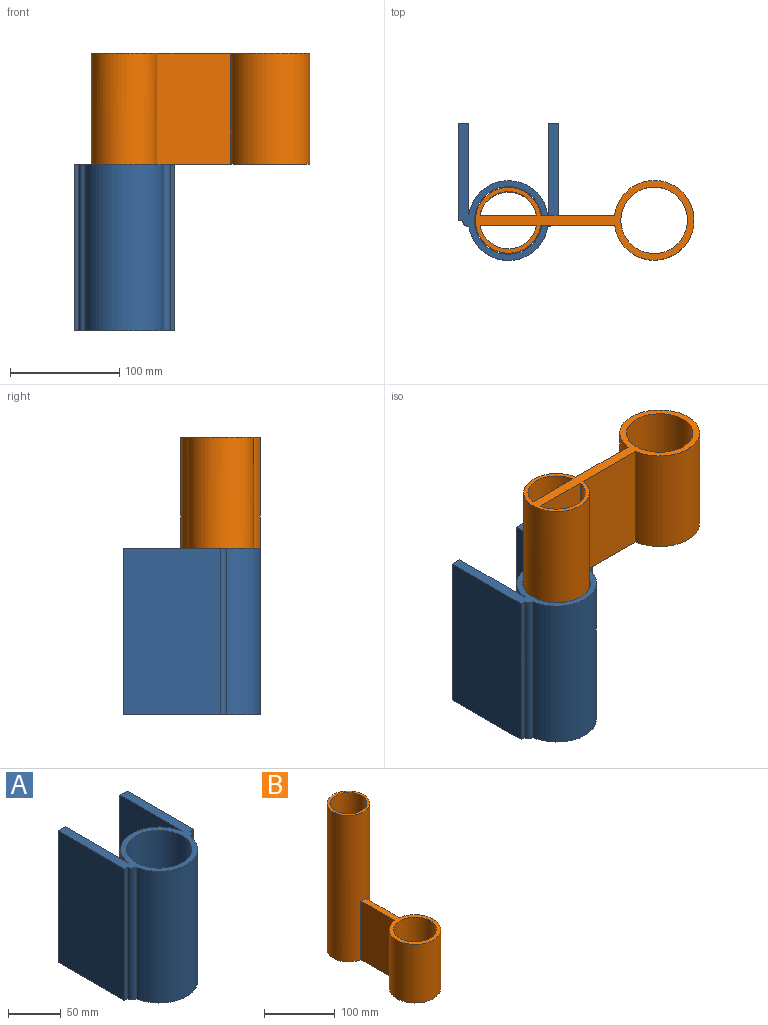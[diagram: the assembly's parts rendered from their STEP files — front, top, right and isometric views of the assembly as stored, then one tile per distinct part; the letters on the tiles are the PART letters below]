
ASSEMBLY  parts=2 mates=1
PART A: 17 faces, bbox 92.1x125.4x152.4 mm
  f0: cylinder r=36.51mm len=152.4mm, axis (0,0,1), area 15840.5mm2, adj f3,f9,f10,f16
  f1: cylinder r=30.96mm len=152.4mm, axis (0,0,1), area 29642.4mm2, adj f3,f16
  f2: cylinder r=36.51mm len=152.4mm, axis (0,0,1), area 15840.5mm2, adj f3,f4,f15,f16
  f3: plane 125.41x92.08mm, normal (0,0,-1), area 2919.4mm2, adj f0,f1,f2,f4,f5,f6,f7,f8
  f4: cylinder r=5.34mm len=152.4mm, axis (0,0,1), area 1335.1mm2, adj f2,f3,f5,f16
  f5: plane 152.4x4.2mm, normal (0,-1,0), area 640.5mm2, adj f3,f4,f8,f16
  f6: plane 152.4x83.56mm, normal (1,0,0), area 12734.6mm2, adj f3,f7,f9,f16
  f7: plane 152.4x9.53mm, normal (0,1,0), area 1451.6mm2, adj f3,f6,f8,f16
  f8: plane 152.4x88.9mm, normal (-1,0,0), area 13548.4mm2, adj f3,f5,f7,f16
  f9: cylinder r=5.34mm len=152.4mm, axis (0,0,1), area 59.6mm2, adj f0,f3,f6,f16
  f10: cylinder r=5.42mm len=152.4mm, axis (0,0,1), area 61.3mm2, adj f0,f3,f11,f16
  f11: plane 152.4x83.48mm, normal (-1,0,0), area 12722.9mm2, adj f3,f10,f14,f16
  f12: plane 152.4x4.11mm, normal (0,-1,0), area 626.2mm2, adj f3,f13,f15,f16
  f13: plane 152.4x88.9mm, normal (1,0,0), area 13548.4mm2, adj f3,f12,f14,f16
  f14: plane 152.4x9.53mm, normal (0,1,0), area 1451.6mm2, adj f3,f11,f13,f16
  f15: cylinder r=5.42mm len=152.4mm, axis (0,0,1), area 1357.9mm2, adj f2,f3,f12,f16
  f16: plane 125.41x92.08mm, normal (0,0,1), area 2919.4mm2, adj f0,f1,f2,f4,f5,f6,f7,f8
PART B: 12 faces, bbox 73x200.2x254 mm
  f0: plane 52.52x9.53mm, normal (0,0,1), area 497.5mm2, adj f2,f4,f5
  f1: cylinder r=30.16mm len=254mm, axis (0,0,-1), area 47165.4mm2, adj f6,f7,f9,f10,f11
  f2: cylinder r=26.26mm len=254mm, axis (0,0,-1), area 39960.4mm2, adj f0,f4,f5,f9,f11
  f3: cylinder r=30.48mm len=101.6mm, axis (0,0,-1), area 19457.6mm2, adj f9,f10
  f4: plane 101.6x51.65mm, normal (1,0,0), area 5247.2mm2, adj f0,f2,f9
  f5: plane 101.6x51.65mm, normal (-1,0,0), area 5247.2mm2, adj f0,f2,f9
  f6: plane 101.6x67.56mm, normal (1,0,0), area 6863.7mm2, adj f1,f8,f9,f10
  f7: plane 101.6x67.56mm, normal (-1,0,0), area 6863.7mm2, adj f1,f8,f9,f10
  f8: cylinder r=36.51mm len=101.6mm, axis (0,0,1), area 22338mm2, adj f6,f7,f9,f10
  f9: plane 200.22x73.03mm, normal (0,0,-1), area 3098.2mm2, adj f1,f2,f3,f4,f5,f6,f7,f8
  f10: plane 140.27x73.03mm, normal (0,0,1), area 1908.7mm2, adj f1,f3,f6,f7,f8
  f11: plane 60.33x60.33mm, normal (0,0,1), area 692mm2, adj f1,f2
PLACE A t=(0,0,152.4)mm
PLACE B rot(axis=(0.71,-0.71,0),180deg) t=(0,0,152.4)mm
MATE revolute B.f2 <-> A.f1  axis (0,0,1) through (0,0,0)mm
